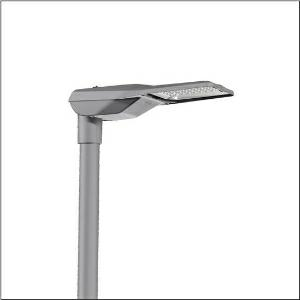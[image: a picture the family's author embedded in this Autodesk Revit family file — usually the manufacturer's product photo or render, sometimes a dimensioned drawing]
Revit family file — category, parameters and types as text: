
# Revit family: streetlight_sl_21_mini___st1_0a_5xe2d33s08jb_3228
name_source: partatom
category: Lighting Fixtures
units: mm (PartAtom-declared; Revit-internal decimal feet)

## family parameters
Cut with Voids When Loaded = No
Host = Face
Light Source = No
Part Type = Normal
Room Calculation Point = No
Round Connector Dimension = Use Diameter
Shared = No

## types (1)
- --- (1 x LED, 12940 lm, 88.6 W, 3000K)
    Apparent Load = 89 VA
    CIE Flux Codes = 40 73 97 100 100
    Color Rendering = 70
    Color Temperature = 3000K
    Default Elevation = 1800 mm
    Description = Streetlight SL 21 mini, mast luminaire, primary light control with lens, of PMMA, primary optical cover: cover, of toughened safety glass, transparent, light distribution: ST1.0a, light emission: direct distribution, primary light characteristic: asymmetric, installation type: side-entry, post-top, LED, High Power LED, rated luminous flux: 12.940lm, luminous efficacy: 146lm/W, light colour: 730, colour temperature: 3000K, control gear: D4i, control: flexible luminous flux parameterisation, time-dependent luminous flux control, constant luminous flux control, overheat protection, pre-setting: logarithmic dimming characteristic, mains connection: 220..240V, AC, 50/60Hz, start of lifetime: 89W, end of service life: 92W, reduction: 41W, luminaire housing, of diecast aluminium, powder-coated, SITECO metallic grey (DB 702S), corrosivity category C5 high according to DIN EN ISO 12944, please order mast flange separately, inclination adjustable: 0°, 5°, 10°, 15°, sealing non-destructively replaceable, multi-level sealing system, length: 628mm, width: 235mm, height: 110mm, mast flange for spigot size: 42mm (side-entry): 5XC10008XM4, 60/48mm (side-entry/post-top): 5XC10108XM2, 76/60mm (side-entry/post-top): 5XC10108XM1, mounting height: 4..8m, Smart Interface above, protection rating (complete): IP66, insulation class (complete): insulation class II (safety insulation), certification: CE, ENEC, ENEC+, VDE, impact resistance: IK10, permissible operating ambient temperature for outdoor applications: -40..+50°C, standard-compliant lighting for roads and squares, packaging unit: 1 piece

Light Distribution: ST1.0a
    Height = 110 mm
    Lamp = 1 x LED
    Lamp Light Flux = 12940 lm
    Lamp Power = 88.6 W
    Lamp count = 1
    Length = 625 mm
    Luminous efficacy = 146 lm/W
    Manufacturer = Siteco
    ModVariant = No
    Model = 5XE2D33S08JB
    Number of Poles = 1
    OnlyDefault = Yes
    Power Factor = 1
    Product Name = Streetlight SL 21 mini | ST1.0a
    Product group = mast luminaire | pylon top
    ProductGroupID = 6100
    Protection Class = Protection class II
    Protection Degree = IP 66
    RLX_Detail_Level = 1
    RLX_Emergency_Light_Flux = 0 lm
    RLX_Emergency_Type = 0
    RLX_Emergency_Type_DB = No
    RlxData = <blob elided: 26337 chars, md5=bef01ad7>
    Socket = socket
    Standby Power = 0 W
    System Light Flux = 12940 lm
    System Power = 89 W
    Type Comments = factory setting: luminous flux: 100 % | dim-lin: 254 | 915 mA
    Type Image = l_1003515.jpg
    URL = http://relux.com
    VarID = @adj_031273
    Voltage = 0 V
    Weight = 0.00 kg
    Width = 234 mm

## geometry (parser evidence)
native form markers: Blend x4, Sweep x13
no freeform markers — native parametric forms only
